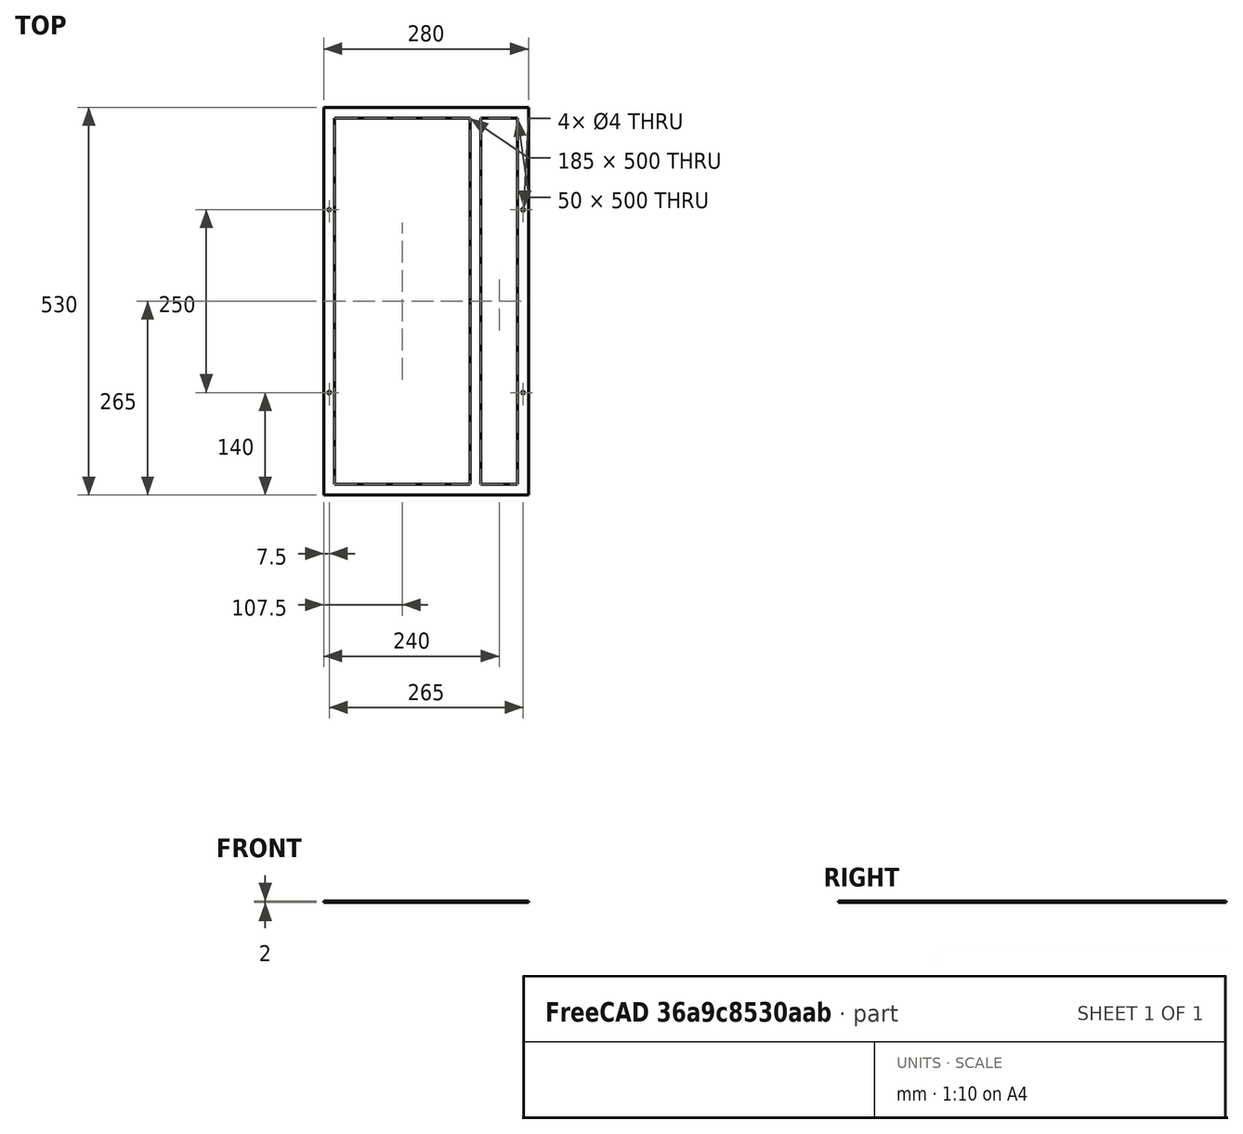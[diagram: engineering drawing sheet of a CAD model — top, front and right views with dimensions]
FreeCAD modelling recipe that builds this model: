
FCSTD DOCUMENT  (FreeCAD 0.16R6698 (Git))
Label: Face_Plate
License: All rights reserved
LicenseURL: http://en.wikipedia.org/wiki/All_rights_reserved
objects: Sketcher::SketchObject×1, PartDesign::Pad×1
note: 3 computed .brp shape members not serialized (recipe doc carries the construction recipe); baked Part::Feature solids carry a one-line shape summary decoded from their .brp

FEATURE [Sketcher::SketchObject] Sketch
  sketch-geometry (16):
    g0: LineSegment StartX=-140 StartY=265 StartZ=0 EndX=140 EndY=265 EndZ=0
    g1: LineSegment StartX=140 StartY=265 StartZ=0 EndX=140 EndY=-265 EndZ=0
    g2: LineSegment StartX=140 StartY=-265 StartZ=0 EndX=-140 EndY=-265 EndZ=0
    g3: LineSegment StartX=-140 StartY=-265 StartZ=0 EndX=-140 EndY=265 EndZ=0
    g4: LineSegment StartX=-125 StartY=250 StartZ=0 EndX=60 EndY=250 EndZ=0
    g5: LineSegment StartX=60 StartY=250 StartZ=0 EndX=60 EndY=-250 EndZ=0
    g6: LineSegment StartX=60 StartY=-250 StartZ=0 EndX=-125 EndY=-250 EndZ=0
    g7: LineSegment StartX=-125 StartY=-250 StartZ=0 EndX=-125 EndY=250 EndZ=0
    g8: LineSegment StartX=75 StartY=250 StartZ=0 EndX=125 EndY=250 EndZ=0
    g9: LineSegment StartX=125 StartY=250 StartZ=0 EndX=125 EndY=-250 EndZ=0
    g10: LineSegment StartX=125 StartY=-250 StartZ=0 EndX=75 EndY=-250 EndZ=0
    g11: LineSegment StartX=75 StartY=-250 StartZ=0 EndX=75 EndY=250 EndZ=0
    g12: Circle CenterX=-132.5 CenterY=125 CenterZ=0 NormalX=0 NormalY=0 NormalZ=1 Radius=2
    g13: Circle CenterX=-132.5 CenterY=-125 CenterZ=0 NormalX=0 NormalY=0 NormalZ=1 Radius=2
    g14: Circle CenterX=132.5 CenterY=-125 CenterZ=0 NormalX=0 NormalY=0 NormalZ=1 Radius=2
    g15: Circle CenterX=132.5 CenterY=125 CenterZ=0 NormalX=0 NormalY=0 NormalZ=1 Radius=2
  constraints (48):
    c: Coincident(g0,g1)
    c: Coincident(g1,g2)
    c: Coincident(g2,g3)
    c: Coincident(g3,g0)
    c: Horizontal(g0)
    c: Horizontal(g2)
    c: Vertical(g1)
    c: Vertical(g3)
    c: DistanceX(g0,g0) = 280
    c: DistanceY(g3,g3) = 530
    c: Coincident(g4,g5)
    c: Coincident(g5,g6)
    c: Coincident(g6,g7)
    c: Coincident(g7,g4)
    c: Horizontal(g4)
    c: Horizontal(g6)
    c: Vertical(g5)
    c: Vertical(g7)
    c: Coincident(g8,g9)
    c: Coincident(g9,g10)
    c: Coincident(g10,g11)
    c: Coincident(g11,g8)
    c: Horizontal(g8)
    c: Horizontal(g10)
    c: Vertical(g9)
    c: Vertical(g11)
    c: DistanceY(g9,g9) = 500
    c: DistanceY(g8,g0) = 15
    c: DistanceY(g4,g8) = 0
    c: DistanceY(g10,g5) = 0
    c: DistanceX(g5,g10) = 15
    c: DistanceX(g2,g6) = 15
    c: DistanceX(g9,g1) = 15
    c: DistanceX(g4,g4) = 185
    c: DistanceY(g-1,g0) = 265
    c: DistanceX(g0,g-1) = 140
    c: Radius(g15) = 2
    c: Equal(g15,g12)
    c: Equal(g15,g13)
    c: Equal(g15,g14)
    c: DistanceY(g13,g12) = 250
    c: DistanceX(g0,g12) = 7.5
    c: DistanceX(g12,g13) = 0
    c: DistanceY(g12,g0) = 140
    c: DistanceY(g15,g0) = 140
    c: DistanceY(g14,g15) = 250
    c: DistanceX(g14,g15) = 0
    c: DistanceX(g15,g0) = 7.5
FEATURE [PartDesign::Pad] Pad
  Length = 2
  Length2 = 100
  Sketch = -> Sketch
  Type = 0
